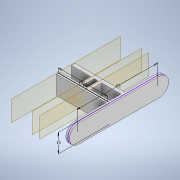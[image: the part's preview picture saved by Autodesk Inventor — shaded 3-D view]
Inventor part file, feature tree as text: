
AUTODESK INVENTOR PART (.ipt)
format: ipt  version: 2020 (Build 240168000, 168)  size: 154,624 bytes
history: native  units: mm
features: sketch x5, plane x5, extrude x5
ambient origin geometry x8: Origin, YZ Plane, XZ Plane, XY Plane, X Axis, Y Axis, Z Axis, Center Point
bodies: Solid1 (feature_tree)
feature tree (15):
  sketch  "Sketch1"  dims[d25=65.0mm d26=15.0mm]
  plane  "Work Plane1"
  plane  "Work Plane2"
  extrude  "Extrusion1"  Depth=15.0mm
  sketch  "Sketch2"  dims[d27=6.0mm d28=3.0mm d29=0.0mm]
  sketch  "Sketch3"  dims[d30=40.0mm d31=3.0mm]
  plane  "Work Plane5"
  plane  "Work Plane6"
  plane  "Work Plane7"
  sketch  "Sketch5"  dims[d32=3.0mm d35=40.0mm]
  sketch  "Sketch6"  dims[d39=-18.5mm d42=6.0mm d43=6.0mm d44=6.0mm d45=3.0mm d46=0.0mm d47=3.0mm d48=0.0mm d49=3.0mm d50=0.0mm d51=3.0mm d52=0.0mm d4=0.5mm d5=0.872665mm d6=0.5mm d7=0.872665mm]
  extrude  "Extrusion2"  Depth=3.0mm TaperAngle=0.0deg
  extrude  "Extrusion3"  Depth=3.0mm
  extrude  "Extrusion4"  Depth=40.0mm
  extrude  "Extrusion5"  Depth=6.0mm
